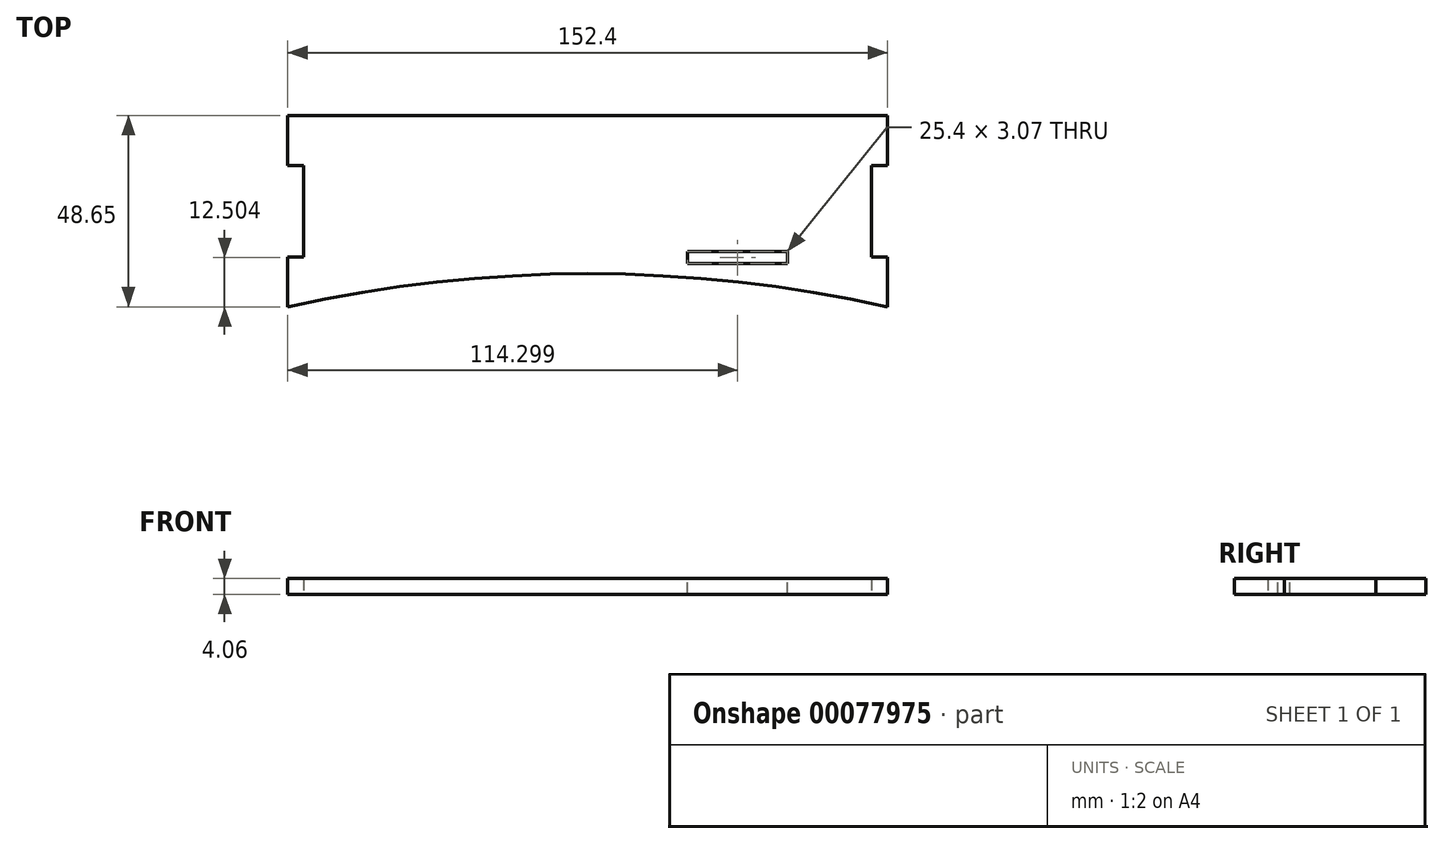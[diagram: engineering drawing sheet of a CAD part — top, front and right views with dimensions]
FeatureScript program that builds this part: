
annotation { "Feature Type Name" : "Feature", "Feature Type Description" : "" }
export const myFeature = defineFeature(function(context is Context, id is Id, definition is map)
    precondition{}
    {
        {
            var Q0;
            Q0=qCreatedBy(makeId("Top.planeOp"),FACE);
            var sketch = newSketch(context, id + "F0", { "sketchPlane" : qUnion([Q0])});
            skPoint(sketch, "E0.orphan", {"position": v(-104.54, -74.89) * mm});
            skPoint(sketch, "E1.start.orphan", {"position": v(-26.76, -57.56) * mm});
            skPoint(sketch, "E2.start.orphan", {"position": v(-93.43, -57.56) * mm});
            skPoint(sketch, "E3.MirrorCS.end.orphan", {"position": v(39.92, -57.56) * mm});
            skPoint(sketch, "E4.right.end.orphan", {"position": v(51.03, -74.89) * mm});
            skLineSegment(sketch, "E5", {"start": v(-93.43, -74.89) * mm, "end": v(-93.43, -62.19) * mm});
            skLineSegment(sketch, "E6", {"start": v(58.97, -74.89) * mm, "end": v(58.97, -62.19) * mm});
            skLineSegment(sketch, "E7", {"start": v(-89.37, -62.19) * mm, "end": v(-93.43, -62.19) * mm});
            skLineSegment(sketch, "E8", {"start": v(-89.37, -62.19) * mm, "end": v(-89.37, -38.94) * mm});
            skLineSegment(sketch, "E9.MirrorCS", {"start": v(54.9, -62.19) * mm, "end": v(54.9, -38.94) * mm});
            skLineSegment(sketch, "E10.MirrorCS", {"start": v(54.9, -62.19) * mm, "end": v(58.97, -62.19) * mm});
            skLineSegment(sketch, "E11.trimOffspring", {"start": v(58.97, -36.79) * mm, "end": v(58.97, -26.24) * mm});
            skPoint(sketch, "E12.end.orphan", {"position": v(-17.23, -74.89) * mm});
            skArc(sketch, "E13", {"start": v(58.97, -74.89) * mm, "mid": v(-17.23, -66.45) * mm, "end": v(-93.43, -74.89) * mm});
            skLineSegment(sketch, "E14", {"start": v(54.9, -26.24) * mm, "end": v(58.97, -26.24) * mm});
            skPoint(sketch, "E14.endSnap0", {"position": v(58.97, -30.44) * mm});
            skLineSegment(sketch, "E15", {"start": v(58.97, -26.24) * mm, "end": v(58.97, -38.94) * mm});
            skLineSegment(sketch, "E16", {"start": v(58.97, -38.94) * mm, "end": v(54.9, -38.94) * mm});
            skPoint(sketch, "E17.orphan", {"position": v(58.97, -24.09) * mm});
            skLineSegment(sketch, "E18", {"start": v(54.9, -26.24) * mm, "end": v(-93.43, -26.24) * mm});
            skLineSegment(sketch, "E19", {"start": v(-93.43, -26.24) * mm, "end": v(-93.43, -38.94) * mm});
            skLineSegment(sketch, "E20", {"start": v(-93.43, -38.94) * mm, "end": v(-89.37, -38.94) * mm});
            skSolve(sketch);
        }
        {
            var Q0;
            Q0=qSketchRegion(id+"F0",true);
            extrude(context, id + "F1", {"entities" : qUnion([Q0]), "depth" : 4.06 * mm});
        }
        {
            var Q0;
            Q0=makeQuery(id+"F1.opExtrude","CAP_FACE",FACE,{"disambiguationData":[OSD([sQuery(id+"F0.wireOp",EDGE,"E5"),sQuery(id+"F0.wireOp",EDGE,"E6"),sQuery(id+"F0.wireOp",EDGE,"E7"),sQuery(id+"F0.wireOp",EDGE,"E8"),sQuery(id+"F0.wireOp",EDGE,"E9.MirrorCS"),sQuery(id+"F0.wireOp",EDGE,"E10.MirrorCS"),sQuery(id+"F0.wireOp",EDGE,"E13"),sQuery(id+"F0.wireOp",EDGE,"E14"),sQuery(id+"F0.wireOp",EDGE,"E15"),sQuery(id+"F0.wireOp",EDGE,"E16"),sQuery(id+"F0.wireOp",EDGE,"E18"),sQuery(id+"F0.wireOp",EDGE,"E19"),sQuery(id+"F0.wireOp",EDGE,"E20")])],"isStart":false});
            var sketch = newSketch(context, id + "F2", { "sketchPlane" : qUnion([Q0])});
            skLineSegment(sketch, "E21", {"start": v(-17.23, -66.45) * mm, "end": v(-17.23, -58.94) * mm});
            skLineSegment(sketch, "E22", {"start": v(-42.63, -63.92) * mm, "end": v(-42.63, -67.38) * mm});
            skLineSegment(sketch, "E23", {"start": v(-42.63, -63.92) * mm, "end": v(-68.03, -63.92) * mm});
            skLineSegment(sketch, "E24", {"start": v(-42.63, -63.92) * mm, "end": v(-42.63, -60.85) * mm});
            skLineSegment(sketch, "E25.bottom", {"start": v(-68.03, -63.92) * mm, "end": v(-42.63, -63.92) * mm});
            skLineSegment(sketch, "E25.top", {"start": v(-68.03, -60.85) * mm, "end": v(-42.63, -60.85) * mm});
            skLineSegment(sketch, "E25.left", {"start": v(-68.03, -63.92) * mm, "end": v(-68.03, -60.85) * mm});
            skLineSegment(sketch, "E26.MirrorCS", {"start": v(33.57, -60.85) * mm, "end": v(8.17, -60.85) * mm});
            skLineSegment(sketch, "E27.MirrorCS", {"start": v(8.17, -63.92) * mm, "end": v(8.17, -60.85) * mm});
            skLineSegment(sketch, "E28.MirrorCS", {"start": v(33.57, -63.92) * mm, "end": v(8.17, -63.92) * mm});
            skLineSegment(sketch, "E29.MirrorCS", {"start": v(33.57, -63.92) * mm, "end": v(33.57, -60.85) * mm});
            skSolve(sketch);
        }
        {
            var Q0;
            Q0=makeQuery(id+"F2.imprint","IMPRINT",FACE,{"disambiguationData":[TD([[makeQuery(id+"F2.imprint","IMPRINT",EDGE,{"derivedFrom":sQuery(id+"F2.wireOp",EDGE,"E26.MirrorCS")}),1.0]])]});
            var Q1;
            Q1=makeQuery(id+"F2.imprint","IMPRINT",FACE,{"disambiguationData":[TD([[makeQuery(id+"F2.imprint","IMPRINT",EDGE,{"derivedFrom":sQuery(id+"F2.wireOp",EDGE,"E25.bottom")}),1.0]])]});
            extrude(context, id + "F3", {"entities" : qUnion([Q0, Q1]), "operationType" : NewBodyOperationType.REMOVE, "oppositeDirection" : true, "depth" : 25.4 * mm});
        }
    });
